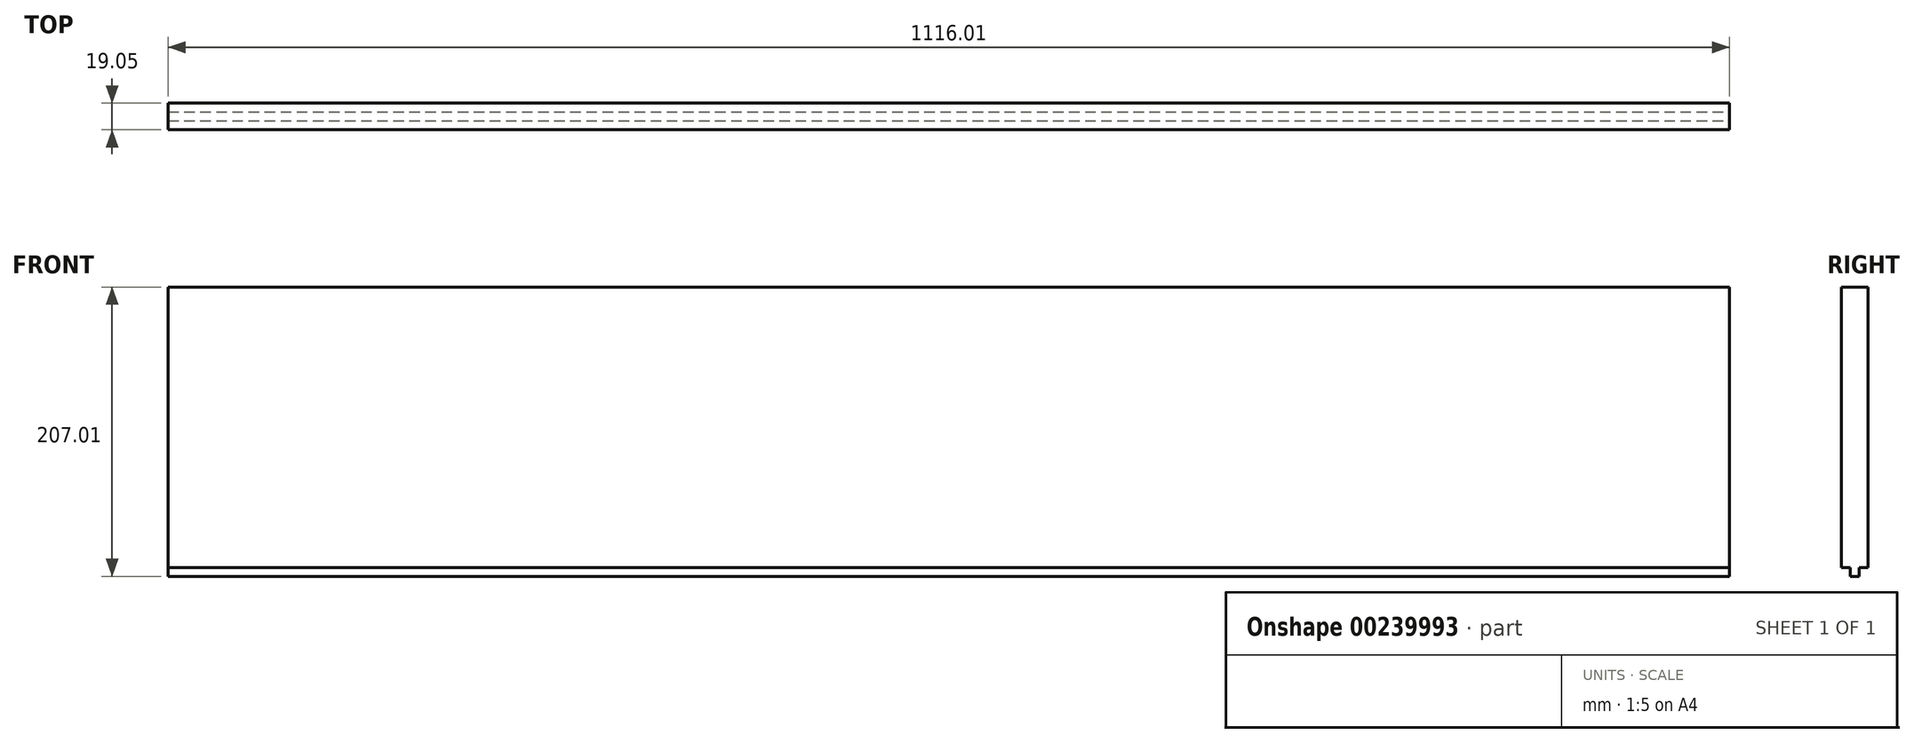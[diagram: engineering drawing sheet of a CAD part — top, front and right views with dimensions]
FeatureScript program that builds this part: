
annotation { "Feature Type Name" : "Feature", "Feature Type Description" : "" }
export const myFeature = defineFeature(function(context is Context, id is Id, definition is map)
    precondition{}
    {
        {
            var Q0;
            Q0=qCreatedBy(makeId("Front.planeOp"),FACE);
            var sketch = newSketch(context, id + "F0", { "sketchPlane" : qUnion([Q0])});
            skLineSegment(sketch, "E0.bottom", {"start": v(-599.98, -295.78) * mm, "end": v(516.03, -295.78) * mm});
            skLineSegment(sketch, "E0.top", {"start": v(-599.98, -502.8) * mm, "end": v(516.03, -502.8) * mm});
            skLineSegment(sketch, "E0.left", {"start": v(-599.98, -295.78) * mm, "end": v(-599.98, -502.8) * mm});
            skLineSegment(sketch, "E0.right", {"start": v(516.03, -295.78) * mm, "end": v(516.03, -502.8) * mm});
            skSolve(sketch);
        }
        {
            var Q0;
            Q0=makeQuery(id+"F0.imprint","IMPRINT",FACE,{"disambiguationData":[TD([[makeQuery(id+"F0.imprint","IMPRINT",EDGE,{"derivedFrom":sQuery(id+"F0.wireOp",EDGE,"E0.bottom")}),-1.0]])]});
            extrude(context, id + "F1", {"entities" : qUnion([Q0]), "depth" : 19.05 * mm, "offsetDistance" : 25.4 * mm});
        }
        {
            var Q0;
            Q0=makeQuery(id+"F1.opExtrude","SWEPT_FACE",FACE,{"disambiguationData":[OSD([sQuery(id+"F0.wireOp",EDGE,"E0.right")])]});
            var sketch = newSketch(context, id + "F2", { "sketchPlane" : qUnion([Q0])});
            skLineSegment(sketch, "E1.bottom", {"start": v(-19.05, -496.44) * mm, "end": v(-12.7, -496.44) * mm});
            skLineSegment(sketch, "E1.top", {"start": v(-19.05, -502.8) * mm, "end": v(-12.7, -502.8) * mm});
            skLineSegment(sketch, "E1.left", {"start": v(-19.05, -496.44) * mm, "end": v(-19.05, -502.8) * mm});
            skLineSegment(sketch, "E1.right", {"start": v(-12.7, -496.44) * mm, "end": v(-12.7, -502.8) * mm});
            skLineSegment(sketch, "E2.bottom", {"start": v(-6.35, -496.44) * mm, "end": v(0, -496.44) * mm});
            skLineSegment(sketch, "E2.top", {"start": v(-6.35, -502.8) * mm, "end": v(0, -502.8) * mm});
            skLineSegment(sketch, "E2.left", {"start": v(-6.35, -496.44) * mm, "end": v(-6.35, -502.8) * mm});
            skLineSegment(sketch, "E2.right", {"start": v(0, -496.44) * mm, "end": v(0, -502.8) * mm});
            skSolve(sketch);
        }
        {
            var Q0;
            Q0=makeQuery(id+"F2.imprint","IMPRINT",FACE,{"disambiguationData":[TD([[makeQuery(id+"F2.imprint","IMPRINT",EDGE,{"derivedFrom":sQuery(id+"F2.wireOp",EDGE,"E1.bottom")}),-1.0]])]});
            var Q1;
            Q1=makeQuery(id+"F2.imprint","IMPRINT",FACE,{"disambiguationData":[TD([[makeQuery(id+"F2.imprint","IMPRINT",EDGE,{"derivedFrom":sQuery(id+"F2.wireOp",EDGE,"E2.bottom")}),-1.0]])]});
            extrude(context, id + "F3", {"entities" : qUnion([Q0, Q1]), "operationType" : NewBodyOperationType.REMOVE, "endBound" : BoundingType.THROUGH_ALL, "oppositeDirection" : true, "depth" : 25.4 * mm, "offsetDistance" : 25.4 * mm});
        }
    });
